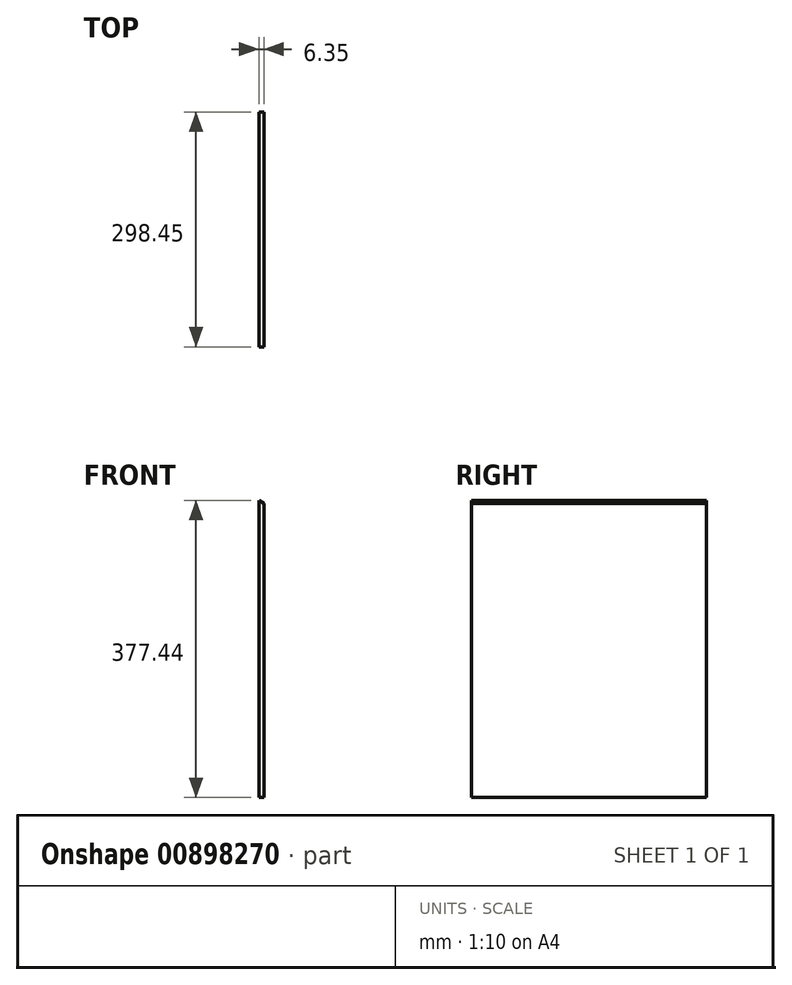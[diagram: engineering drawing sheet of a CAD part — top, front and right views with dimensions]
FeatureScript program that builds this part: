
annotation { "Feature Type Name" : "Feature", "Feature Type Description" : "" }
export const myFeature = defineFeature(function(context is Context, id is Id, definition is map)
    precondition{}
    {
        {
            var Q0;
            Q0=qCreatedBy(makeId("Front.planeOp"),FACE);
            var sketch = newSketch(context, id + "F0", { "sketchPlane" : qUnion([Q0])});
            skLineSegment(sketch, "E0.bottom", {"start": v(0, 0) * mm, "end": v(-6.35, 0) * mm});
            skLineSegment(sketch, "E0.left", {"start": v(0, 0) * mm, "end": v(0, 373.86) * mm});
            skLineSegment(sketch, "E0.right", {"start": v(-6.35, 0) * mm, "end": v(-6.35, 377.44) * mm});
            skLineSegment(sketch, "E1", {"start": v(-6.35, 377.44) * mm, "end": v(0, 373.86) * mm});
            skSolve(sketch);
        }
        {
            var Q0;
            Q0 = qSketchRegion(id + "F0", true);
            extrude(context, id + "F1", {"entities" : qUnion([Q0]), "oppositeDirection" : true, "depth" : 298.45 * mm, "offsetDistance" : 25.4 * mm});
        }
    });
